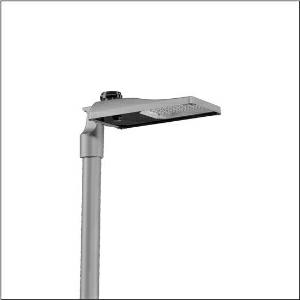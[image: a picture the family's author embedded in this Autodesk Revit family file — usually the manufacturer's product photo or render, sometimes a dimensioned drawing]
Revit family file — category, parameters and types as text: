
# Revit family: streetlight_sl_31_mini___st1_0a_5xh2d3bm08ha_2d93
name_source: partatom
category: Lighting Fixtures
units: mm (PartAtom-declared; Revit-internal decimal feet)

## family parameters
Cut with Voids When Loaded = No
Host = Face
Light Source = No
Part Type = Normal
Room Calculation Point = No
Round Connector Dimension = Use Diameter
Shared = No

## types (1)
- --- (1 x LED, 9230 lm, 68.3 W, 3000K)
    Apparent Load = 68 VA
    CIE Flux Codes = 37 72 97 100 100
    Color Rendering = 70
    Color Temperature = 3000K
    Default Elevation = 1800 mm
    Description = Streetlight SL 31 mini NEMA (7pin) mast luminaire for post-top, side-entry; light control with lens of PMMA; light distribution: ST1.0a, direct asymmetric distribution, for standard-compliant lighting for roads and squares; LED: luminous flux: 9.230lm, light colour: 730, colour temperature: 3000K; luminous efficacy: 135,1lm/W; control: pre-setting: linear dimming characteristic, flexible luminous flux parameterisation, time-dependent luminous flux control, constant luminous flux control, intelligent temperature release in ECG and LED module, overheat protection; luminaire housing, of diecast aluminium, Siteco® metallic grey (DB 702S), corrosivity category C5 high according to DIN EN ISO 12944; cover of toughened safety glass, transparent, mast flange of diecast aluminium, Siteco® metallic grey (DB 702S), spigot size: 76/60mm, mast flange included unmounted; with cable H07RN-F 3x 1.5mm², cable length: 8,5m, connection cable pre-assembled; mains connection: 220..240V, AC, 50/60Hz; power consumption (at start of service life): 68,3W / (at end of service life): 74,5W / (with reduced operation 50%): 29,5W; protection rating (complete): IP66; insulation class (complete): insulation class I (protective earthing); impact resistance: IK09; certification: CE, ENEC, ENEC+, VDE, UKCA; permissible operating ambient temperature for outdoor applications: -40..+50°C; packaging unit: 1 piece

Light Distribution: ST1.0a
    Height = 76 mm
    Lamp = 1 x LED
    Lamp Light Flux = 9230 lm
    Lamp Power = 68.3 W
    Lamp count = 1
    Length = 547 mm
    Luminous efficacy = 135 lm/W
    Manufacturer = Siteco
    ModVariant = No
    Model = 5XH2D3BM08HA
    Number of Poles = 1
    OnlyDefault = Yes
    Power Factor = 1
    Product Name = Streetlight SL 31 mini | ST1.0a
    Product group = mast luminaire | pylon top
    ProductGroupID = 6100
    Protection Class = Protection class I
    Protection Degree = IP 66
    RLX_Detail_Level = 1
    RLX_Emergency_Light_Flux = 0 lm
    RLX_Emergency_Type = 0
    RLX_Emergency_Type_DB = No
    RlxData = <blob elided: 24829 chars, md5=4dd984bb>
    Socket = socket
    Standby Power = 0 W
    System Light Flux = 9230 lm
    System Power = 68 W
    Type Comments = factory setting: luminous flux: 100 % | dim-lin: 254 | 692 mA
    Type Image = l_1300324.jpg
    URL = http://relux.com
    VarID = @adj_002097
    Voltage = 0 V
    Weight = 0.00 kg
    Width = 265 mm

## geometry (parser evidence)
native form markers: Blend x4, Sweep x11
no freeform markers — native parametric forms only
